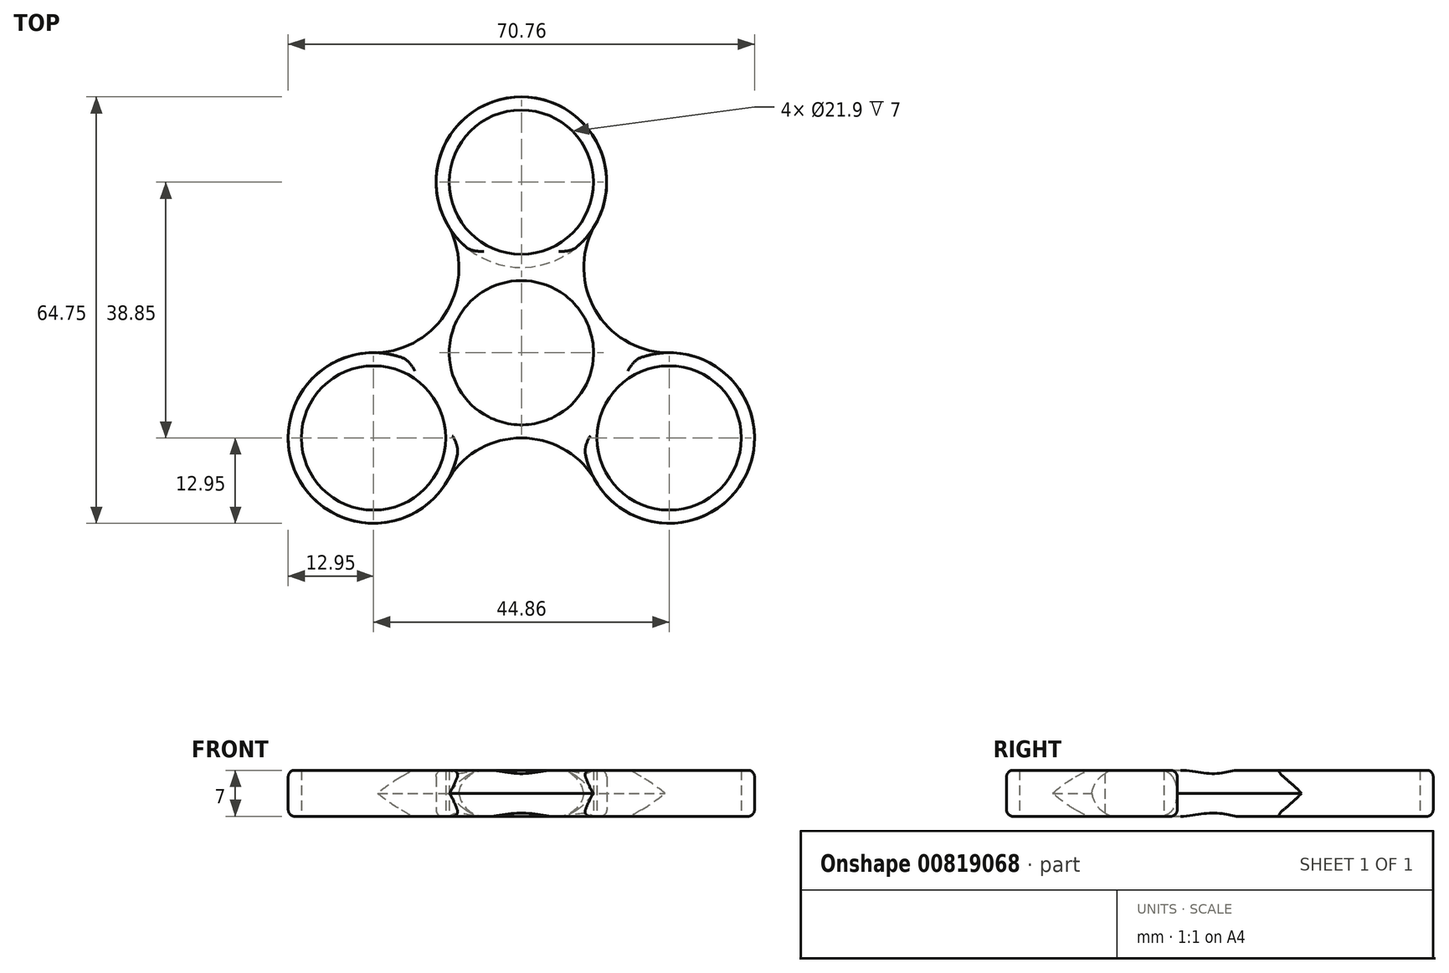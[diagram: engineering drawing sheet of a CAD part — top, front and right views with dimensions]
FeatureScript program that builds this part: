
annotation { "Feature Type Name" : "Feature", "Feature Type Description" : "" }
export const myFeature = defineFeature(function(context is Context, id is Id, definition is map)
    precondition{}
    {
        {
            var Q0;
            Q0=qCreatedBy(makeId("Top.planeOp"),FACE);
            var sketch = newSketch(context, id + "F0", { "sketchPlane" : qUnion([Q0])});
            skCircle(sketch, "E0", {"center": v(0, 0) * mm, "radius": 10.95 * mm});
            skCircle(sketch, "E1.0", {"center": v(0, 0) * mm, "radius": 12.95 * mm});
            skCircle(sketch, "E2", {"center": v(0, 25.9) * mm, "radius": 10.95 * mm});
            skCircle(sketch, "E3.0", {"center": v(0, 25.9) * mm, "radius": 12.95 * mm});
            skCircle(sketch, "E4.1.0", {"center": v(-22.43, -12.95) * mm, "radius": 12.95 * mm});
            skCircle(sketch, "E4.1.1", {"center": v(-22.43, -12.95) * mm, "radius": 10.95 * mm});
            skCircle(sketch, "E4.2.0", {"center": v(22.43, -12.95) * mm, "radius": 12.95 * mm});
            skCircle(sketch, "E4.2.1", {"center": v(22.43, -12.95) * mm, "radius": 10.95 * mm});
            skArc(sketch, "E5", {"start": v(11.22, 19.43) * mm, "mid": v(11.24, 6.5) * mm, "end": v(22.43, 0) * mm});
            skPoint(sketch, "E5.startSnap0", {"position": v(11.22, 6.48) * mm});
            skArc(sketch, "E6.1.0", {"start": v(-22.43, 0) * mm, "mid": v(-11.24, 6.5) * mm, "end": v(-11.22, 19.43) * mm});
            skArc(sketch, "E6.2.0", {"start": v(11.22, -19.43) * mm, "mid": v(0, -12.98) * mm, "end": v(-11.22, -19.43) * mm});
            skSolve(sketch);
        }
        {
            var Q0;
            Q0 = qSketchRegion(id + "F0", true);
            var Q1;
            Q1=makeQuery(id+"F0.imprint","IMPRINT",FACE,{"disambiguationData":[TD([[makeQuery(id+"F0.imprint","IMPRINT",EDGE,{"derivedFrom":sQuery(id+"F0.wireOp",EDGE,"E0")}),-1.0]])]});
            extrude(context, id + "F1", {"entities" : qUnion([Q0, Q1]), "depth" : 7 * mm, "offsetDistance" : 25 * mm});
        }
        {
            var Q0;
            Q0=makeQuery(id+"F1.opExtrude","CAP_EDGE",EDGE,{"disambiguationData":[OSD([sQuery(id+"F0.wireOp",EDGE,"E6.1.0")])],"isStart":false});
            var Q1;
            Q1=makeQuery(id+"F1.opExtrude","CAP_EDGE",EDGE,{"disambiguationData":[OSD([sQuery(id+"F0.wireOp",EDGE,"E5")])],"isStart":false});
            var Q2;
            Q2=makeQuery(id+"F1.opExtrude","CAP_EDGE",EDGE,{"disambiguationData":[OSD([sQuery(id+"F0.wireOp",EDGE,"E6.2.0")])],"isStart":false});
            var Q3;
            Q3=makeQuery(id+"F1.opExtrude","CAP_EDGE",EDGE,{"disambiguationData":[OSD([sQuery(id+"F0.wireOp",EDGE,"E6.1.0")])],"isStart":true});
            var Q4;
            Q4=makeQuery(id+"F1.opExtrude","CAP_EDGE",EDGE,{"disambiguationData":[OSD([sQuery(id+"F0.wireOp",EDGE,"E5")])],"isStart":true});
            var Q5;
            Q5=makeQuery(id+"F1.opExtrude","CAP_EDGE",EDGE,{"disambiguationData":[OSD([sQuery(id+"F0.wireOp",EDGE,"E6.2.0")])],"isStart":true});
            fillet(context, id + "F2", {"entities" : qUnion([Q0, Q1, Q2, Q3, Q4, Q5]), "radius" : 4 * mm, "tangentPropagation" : true, "allowEdgeOverflow" : false});
        }
        {
            var Q0;
            Q0=makeQuery(id+"F1.opExtrude","CAP_EDGE",EDGE,{"disambiguationData":[OSD([sQuery(id+"F0.wireOp",EDGE,"E3.0")])],"isStart":false});
            var Q1;
            Q1=makeQuery(id+"F1.opExtrude","CAP_EDGE",EDGE,{"disambiguationData":[OSD([sQuery(id+"F0.wireOp",EDGE,"E4.2.0")])],"isStart":false});
            var Q2;
            Q2=makeQuery(id+"F1.opExtrude","CAP_EDGE",EDGE,{"disambiguationData":[OSD([sQuery(id+"F0.wireOp",EDGE,"E4.1.0")])],"isStart":false});
            fillet(context, id + "F3", {"entities" : qUnion([Q0, Q1, Q2]), "radius" : 1 * mm, "tangentPropagation" : true, "allowEdgeOverflow" : false});
        }
        {
            var Q0;
            Q0=makeQuery(id+"F1.opExtrude","CAP_EDGE",EDGE,{"disambiguationData":[OSD([sQuery(id+"F0.wireOp",EDGE,"E3.0")])],"isStart":true});
            var Q1;
            Q1=makeQuery(id+"F1.opExtrude","CAP_EDGE",EDGE,{"disambiguationData":[OSD([sQuery(id+"F0.wireOp",EDGE,"E4.1.0")])],"isStart":true});
            var Q2;
            Q2=makeQuery(id+"F1.opExtrude","CAP_EDGE",EDGE,{"disambiguationData":[OSD([sQuery(id+"F0.wireOp",EDGE,"E4.2.0")])],"isStart":true});
            fillet(context, id + "F4", {"entities" : qUnion([Q0, Q1, Q2]), "radius" : 1 * mm, "tangentPropagation" : true, "allowEdgeOverflow" : false});
        }
    });
